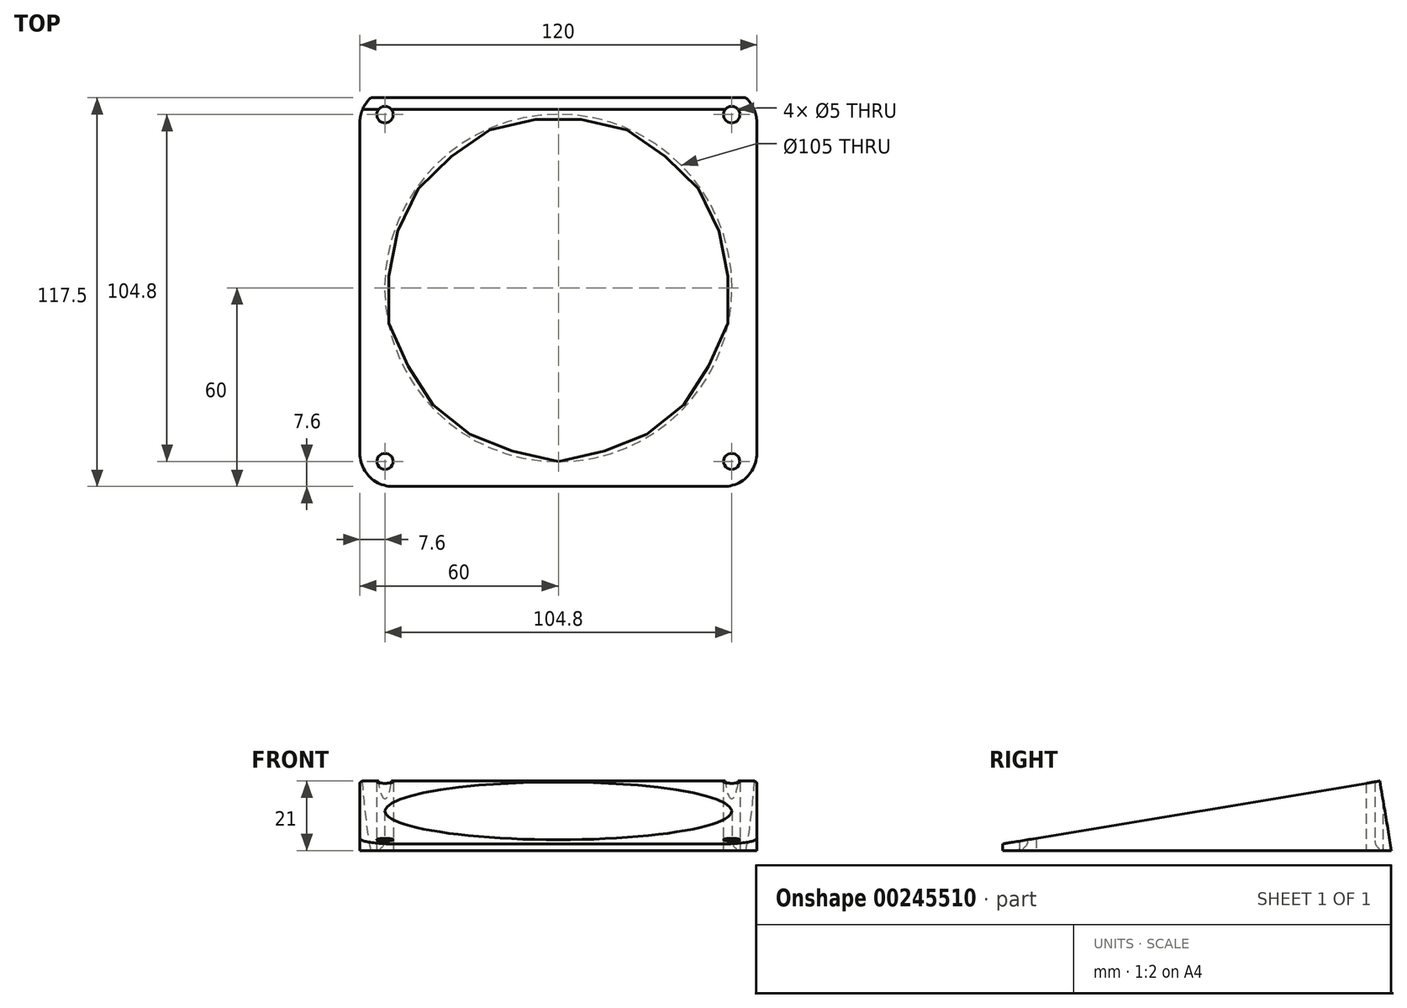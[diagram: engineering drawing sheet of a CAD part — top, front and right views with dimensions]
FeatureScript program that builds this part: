
annotation { "Feature Type Name" : "Feature", "Feature Type Description" : "" }
export const myFeature = defineFeature(function(context is Context, id is Id, definition is map)
    precondition{}
    {
        {
            var Q0;
            Q0=qCreatedBy(makeId("Top.planeOp"),FACE);
            var sketch = newSketch(context, id + "F0", { "sketchPlane" : qUnion([Q0])});
            skLineSegment(sketch, "E0.bottom", {"start": v(10, 0) * mm, "end": v(110, 0) * mm});
            skLineSegment(sketch, "E0.top", {"start": v(10, 120) * mm, "end": v(110, 120) * mm});
            skLineSegment(sketch, "E0.left", {"start": v(0, 10) * mm, "end": v(0, 110) * mm});
            skLineSegment(sketch, "E0.right", {"start": v(120, 10) * mm, "end": v(120, 110) * mm});
            skLineSegment(sketch, "E1", {"start": v(60, 120) * mm, "end": v(60, 0) * mm, "construction": true});
            skCircle(sketch, "E2", {"center": v(60, 60) * mm, "radius": 52.5 * mm});
            skCircle(sketch, "E3", {"center": v(7.6, 7.6) * mm, "radius": 2.5 * mm});
            skLineSegment(sketch, "E4", {"start": v(0, 60) * mm, "end": v(120, 60) * mm, "construction": true});
            skCircle(sketch, "E5.MirrorC", {"center": v(112.4, 7.6) * mm, "radius": 2.5 * mm});
            skCircle(sketch, "E6.MirrorC", {"center": v(7.6, 112.4) * mm, "radius": 2.5 * mm});
            skCircle(sketch, "E7.MirrorC", {"center": v(112.4, 112.4) * mm, "radius": 2.5 * mm});
            skPoint(sketch, "E8.visualSharp", {"position": v(0, 120) * mm});
            skArc(sketch, "E8.filletArc", {"start": v(10, 120) * mm, "mid": v(2.93, 117.07) * mm, "end": v(0, 110) * mm});
            skPoint(sketch, "E9.visualSharp", {"position": v(120, 120) * mm});
            skArc(sketch, "E9.filletArc", {"start": v(120, 110) * mm, "mid": v(117.07, 117.07) * mm, "end": v(110, 120) * mm});
            skPoint(sketch, "E10.visualSharp", {"position": v(120, 0) * mm});
            skArc(sketch, "E10.filletArc", {"start": v(110, 0) * mm, "mid": v(117.07, 2.93) * mm, "end": v(120, 10) * mm});
            skPoint(sketch, "E11.visualSharp", {"position": v(0, 0) * mm});
            skArc(sketch, "E11.filletArc", {"start": v(0, 10) * mm, "mid": v(2.93, 2.93) * mm, "end": v(10, 0) * mm});
            skSolve(sketch);
        }
        {
            var Q0;
            Q0 = qSketchRegion(id + "F0", true);
            extrude(context, id + "F1", {"entities" : qUnion([Q0]), "depth" : 30 * mm});
        }
        {
            var Q0;
            Q0=makeQuery(id+"F1.opExtrude","SWEPT_FACE",FACE,{"disambiguationData":[OSD([sQuery(id+"F0.wireOp",EDGE,"E0.right")])]});
            var sketch = newSketch(context, id + "F2", { "sketchPlane" : qUnion([Q0])});
            skLineSegment(sketch, "E12", {"start": v(0, 2) * mm, "end": v(114, 21) * mm});
            skLineSegment(sketch, "E13", {"start": v(120, 22) * mm, "end": v(120, 45) * mm, "construction": true});
            skLineSegment(sketch, "E14", {"start": v(120, 45) * mm, "end": v(0, 45) * mm});
            skLineSegment(sketch, "E15", {"start": v(0, 45) * mm, "end": v(0, 2) * mm});
            skLineSegment(sketch, "E16", {"start": v(117.5, 0) * mm, "end": v(114, 21) * mm});
            skLineSegment(sketch, "E17", {"start": v(117.5, 0) * mm, "end": v(125, 0) * mm});
            skLineSegment(sketch, "E18", {"start": v(125, 0) * mm, "end": v(125, 45) * mm});
            skLineSegment(sketch, "E19", {"start": v(125, 45) * mm, "end": v(120, 45) * mm});
            skSolve(sketch);
        }
        {
            var Q0;
            Q0 = qSketchRegion(id + "F2", true);
            extrude(context, id + "F3", {"entities" : qUnion([Q0]), "operationType" : NewBodyOperationType.REMOVE, "endBound" : BoundingType.THROUGH_ALL, "oppositeDirection" : true, "depth" : 25 * mm});
        }
        {
            var Q0;
            Q0=makeQuery(id+"F1.opExtrude","CAP_EDGE",EDGE,{"disambiguationData":[OSD([sQuery(id+"F0.wireOp",EDGE,"E2")])],"isStart":true});
            fillet(context, id + "F4", {"entities" : qUnion([Q0]), "radius" : 3 * mm, "tangentPropagation" : true, "allowEdgeOverflow" : false});
        }
    });
